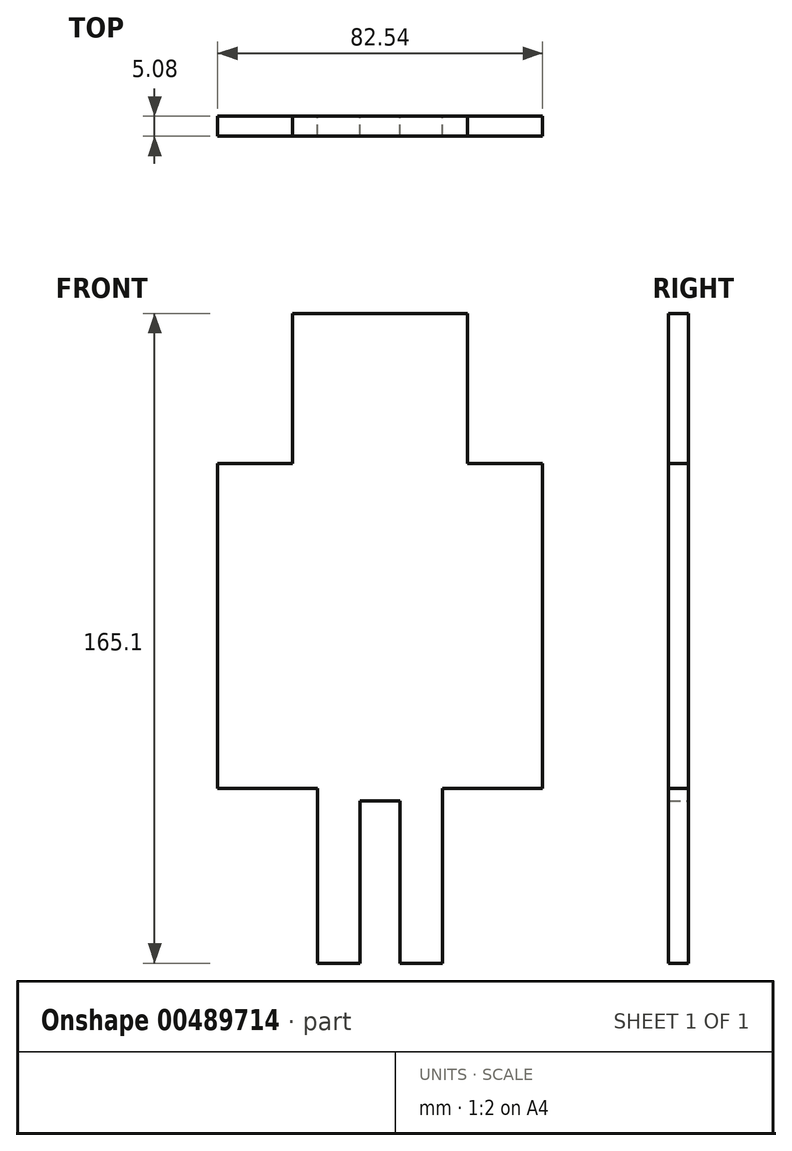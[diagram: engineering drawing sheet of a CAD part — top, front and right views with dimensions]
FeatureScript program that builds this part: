
annotation { "Feature Type Name" : "Feature", "Feature Type Description" : "" }
export const myFeature = defineFeature(function(context is Context, id is Id, definition is map)
    precondition{}
    {
        {
            var Q0;
            Q0=qCreatedBy(makeId("Front.planeOp"),FACE);
            var sketch = newSketch(context, id + "F0", { "sketchPlane" : qUnion([Q0])});
            skLineSegment(sketch, "E0.bottom", {"start": v(-41.27, 41.28) * mm, "end": v(-22.22, 41.28) * mm});
            skLineSegment(sketch, "E0.top", {"start": v(-41.28, -41.28) * mm, "end": v(-15.88, -41.28) * mm});
            skLineSegment(sketch, "E0.left", {"start": v(-41.27, 41.28) * mm, "end": v(-41.28, -41.28) * mm});
            skLineSegment(sketch, "E0.right", {"start": v(41.28, 41.28) * mm, "end": v(41.27, -41.28) * mm});
            skPoint(sketch, "E0.middle", {"position": v(0, 0) * mm});
            skLineSegment(sketch, "E1", {"start": v(-22.22, 41.28) * mm, "end": v(-22.22, 79.38) * mm});
            skLineSegment(sketch, "E2", {"start": v(-22.22, 79.38) * mm, "end": v(22.23, 79.38) * mm});
            skLineSegment(sketch, "E3", {"start": v(22.23, 79.38) * mm, "end": v(22.23, 41.28) * mm});
            skLineSegment(sketch, "E4.trimOffspring", {"start": v(22.23, 41.28) * mm, "end": v(41.28, 41.28) * mm});
            skLineSegment(sketch, "E5", {"start": v(-15.88, -41.28) * mm, "end": v(-15.88, -85.73) * mm});
            skLineSegment(sketch, "E6", {"start": v(-15.88, -85.73) * mm, "end": v(-5.08, -85.73) * mm});
            skLineSegment(sketch, "E7", {"start": v(15.87, -85.73) * mm, "end": v(15.87, -41.28) * mm});
            skLineSegment(sketch, "E8.trimOffspring", {"start": v(15.87, -41.28) * mm, "end": v(41.27, -41.28) * mm});
            skLineSegment(sketch, "E9.bottom", {"start": v(-5.08, -44.45) * mm, "end": v(5.08, -44.45) * mm});
            skLineSegment(sketch, "E9.left", {"start": v(-5.08, -44.45) * mm, "end": v(-5.08, -127) * mm});
            skLineSegment(sketch, "E9.right", {"start": v(5.08, -44.45) * mm, "end": v(5.08, -127) * mm});
            skPoint(sketch, "E9.middle", {"position": v(0, -85.73) * mm});
            skLineSegment(sketch, "E10.trimOffspring", {"start": v(5.08, -85.73) * mm, "end": v(15.87, -85.73) * mm});
            skSolve(sketch);
        }
        {
            var Q0;
            Q0 = qSketchRegion(id + "F0", true);
            extrude(context, id + "F1", {"entities" : qUnion([Q0]), "depth" : 5.08 * mm});
        }
    });
